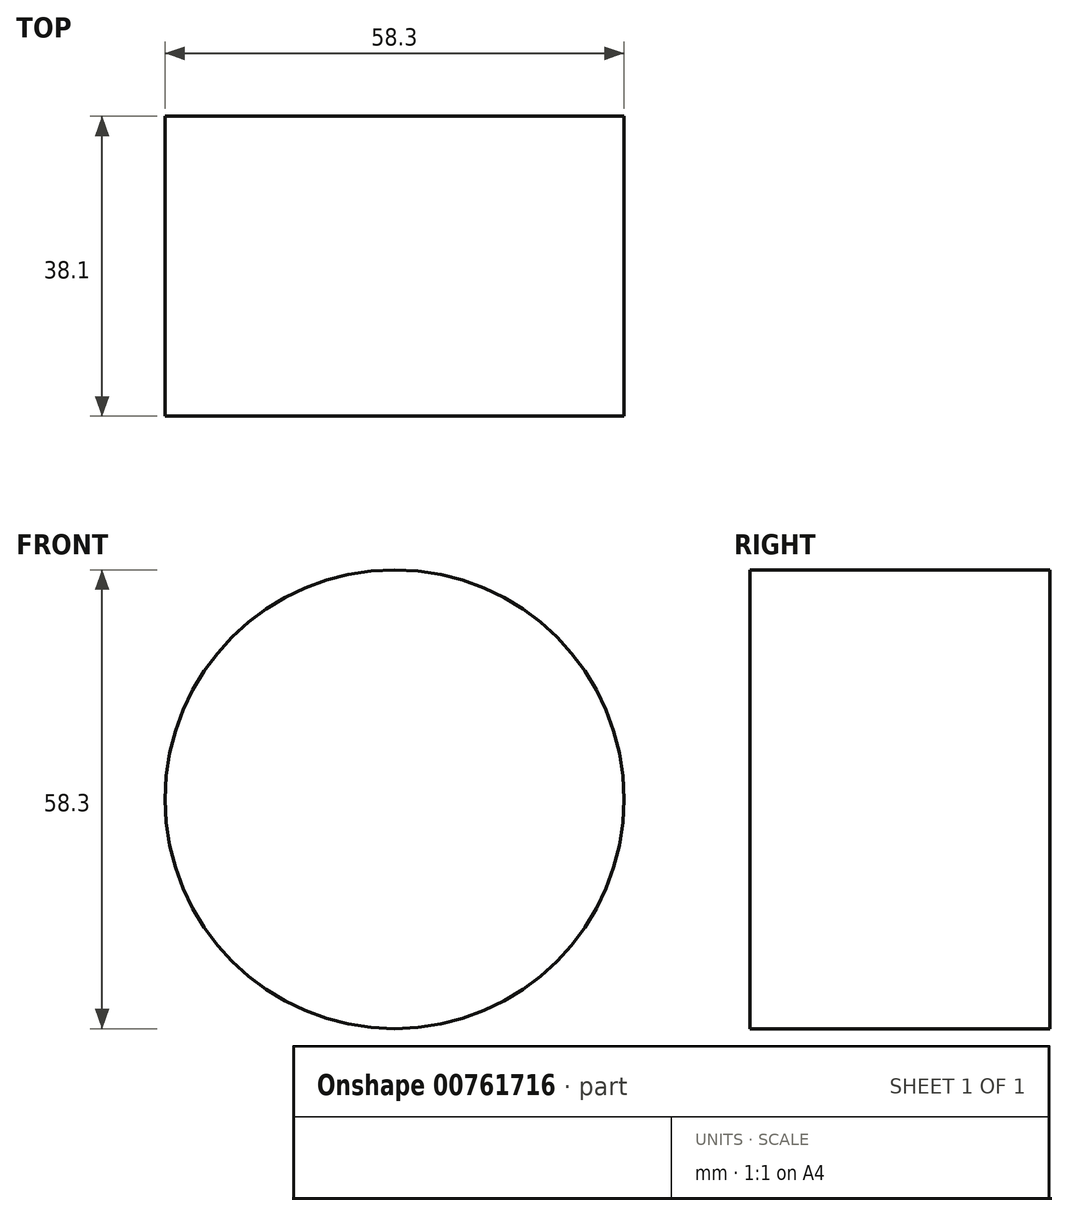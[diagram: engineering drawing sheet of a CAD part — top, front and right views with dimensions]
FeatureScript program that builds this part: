
annotation { "Feature Type Name" : "Feature", "Feature Type Description" : "" }
export const myFeature = defineFeature(function(context is Context, id is Id, definition is map)
    precondition{}
    {
        {
            var Q0;
            Q0=qCreatedBy(makeId("Front.planeOp"),FACE);
            var sketch = newSketch(context, id + "F0", { "sketchPlane" : qUnion([Q0])});
            skCircle(sketch, "E0", {"center": v(0, 0) * mm, "radius": 29.15 * mm});
            skPoint(sketch, "E1.first.point", {"position": v(-29, 13.07) * mm});
            skPoint(sketch, "E1.second.point", {"position": v(29.56, -11.78) * mm});
            skPoint(sketch, "E1.third.point", {"position": v(5.36, -31.36) * mm});
            skSolve(sketch);
        }
        {
            var Q0;
            Q0 = qSketchRegion(id + "F0", true);
            extrude(context, id + "F1", {"entities" : qUnion([Q0]), "depth" : 38.1 * mm, "offsetDistance" : 25.4 * mm});
        }
    });
